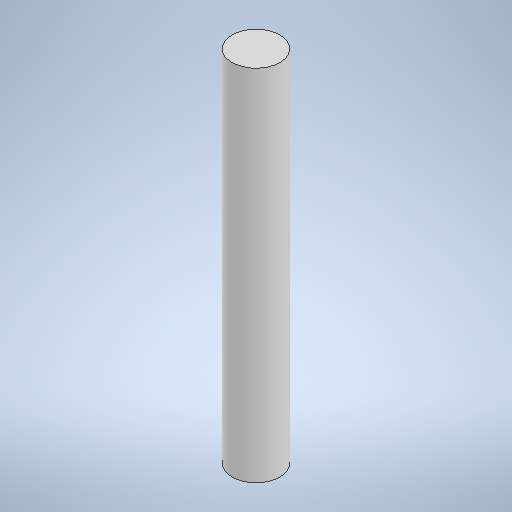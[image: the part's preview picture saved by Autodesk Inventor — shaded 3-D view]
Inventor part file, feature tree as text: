
AUTODESK INVENTOR PART (.ipt)
format: ipt  version: 2025 (Build 290162000, 162)  size: 243,200 bytes
history: native  units: mm
features: extrude x2, sketch x2, other x1
ambient origin geometry x8: Origin, YZ Plane, XZ Plane, XY Plane, X Axis, Y Axis, Z Axis, Center Point
bodies: Body1 (feature_tree)
feature tree (5):
  other  "Bryła1"
  extrude  "Wyciągnięcie proste1"  Depth=10.0mm
  extrude  "Wyciągnięcie proste2"  Depth=75.0mm TaperAngle=0.0deg
  sketch  "Szkic1"
  sketch  "Szkic2"
